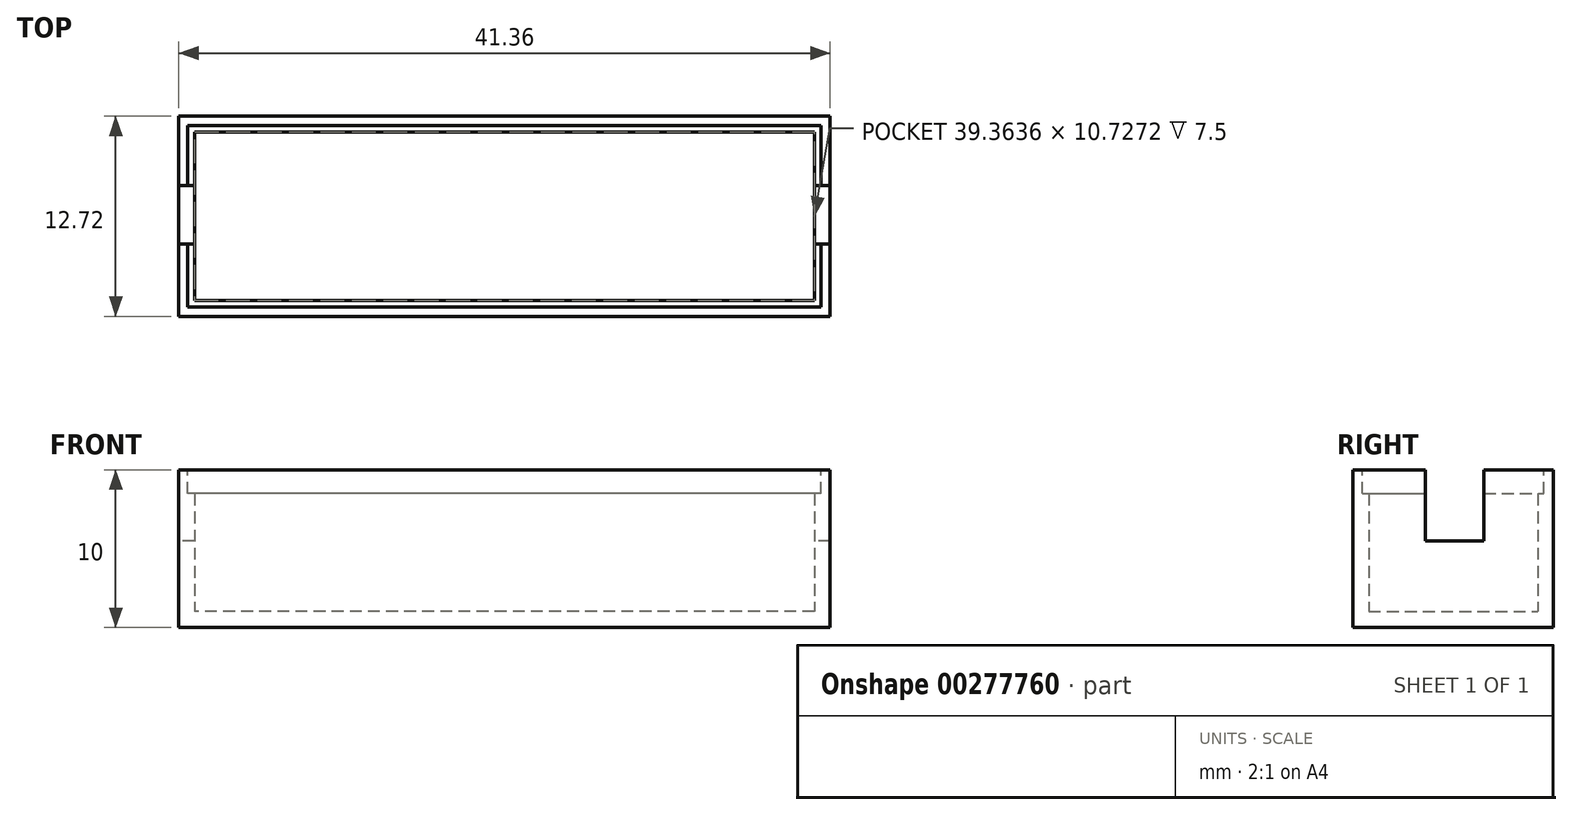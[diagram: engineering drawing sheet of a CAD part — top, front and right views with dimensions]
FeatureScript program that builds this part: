
annotation { "Feature Type Name" : "Feature", "Feature Type Description" : "" }
export const myFeature = defineFeature(function(context is Context, id is Id, definition is map)
    precondition{}
    {
        {
            var Q0;
            Q0=qCreatedBy(makeId("Top.planeOp"),FACE);
            var sketch = newSketch(context, id + "F0", { "sketchPlane" : qUnion([Q0])});
            skLineSegment(sketch, "E0.bottom", {"start": v(20.68, -6.36) * mm, "end": v(-20.68, -6.36) * mm});
            skLineSegment(sketch, "E0.top", {"start": v(20.68, 6.36) * mm, "end": v(-20.68, 6.36) * mm});
            skLineSegment(sketch, "E0.left", {"start": v(20.68, -6.36) * mm, "end": v(20.68, 6.36) * mm});
            skLineSegment(sketch, "E0.right", {"start": v(-20.68, -6.36) * mm, "end": v(-20.68, 6.36) * mm});
            skPoint(sketch, "E0.middle", {"position": v(0, 0) * mm});
            skSolve(sketch);
        }
        {
            var Q0;
            Q0 = qSketchRegion(id + "F0", true);
            extrude(context, id + "F1", {"entities" : qUnion([Q0]), "depth" : 10 * mm});
        }
        {
            var Q0;
            Q0=makeQuery(id+"F1.opExtrude","CAP_FACE",FACE,{"disambiguationData":[OSD([sQuery(id+"F0.wireOp",EDGE,"E0.bottom"),sQuery(id+"F0.wireOp",EDGE,"E0.top"),sQuery(id+"F0.wireOp",EDGE,"E0.left"),sQuery(id+"F0.wireOp",EDGE,"E0.right")])],"isStart":false});
            shell(context, id + "F2", {"entities" : qUnion([Q0]), "thickness" : 1 * mm});
        }
        {
            var Q0;
            Q0=makeQuery(id+"F1.opExtrude","CAP_FACE",FACE,{"disambiguationData":[OSD([sQuery(id+"F0.wireOp",EDGE,"E0.bottom"),sQuery(id+"F0.wireOp",EDGE,"E0.top"),sQuery(id+"F0.wireOp",EDGE,"E0.left"),sQuery(id+"F0.wireOp",EDGE,"E0.right")])],"isStart":false});
            var sketch = newSketch(context, id + "F3", { "sketchPlane" : qUnion([Q0])});
            skLineSegment(sketch, "E1.bottom", {"start": v(20.11, -5.77) * mm, "end": v(-20.11, -5.77) * mm});
            skLineSegment(sketch, "E1.top", {"start": v(20.11, 5.77) * mm, "end": v(-20.11, 5.77) * mm});
            skLineSegment(sketch, "E1.left", {"start": v(20.11, -5.77) * mm, "end": v(20.11, 5.77) * mm});
            skLineSegment(sketch, "E1.right", {"start": v(-20.11, -5.77) * mm, "end": v(-20.11, 5.77) * mm});
            skPoint(sketch, "E1.middle", {"position": v(0, 0) * mm});
            skSolve(sketch);
        }
        {
            var Q0;
            Q0 = qSketchRegion(id + "F3", true);
            extrude(context, id + "F4", {"entities" : qUnion([Q0]), "operationType" : NewBodyOperationType.REMOVE, "oppositeDirection" : true, "depth" : 1.5 * mm});
        }
        {
            var Q0;
            Q0=makeQuery(id+"F1.opExtrude","SWEPT_FACE",FACE,{"disambiguationData":[OSD([sQuery(id+"F0.wireOp",EDGE,"E0.right")])]});
            var sketch = newSketch(context, id + "F5", { "sketchPlane" : qUnion([Q0])});
            skLineSegment(sketch, "E2.bottom", {"start": v(-1.94, 10) * mm, "end": v(1.77, 10) * mm});
            skLineSegment(sketch, "E2.top", {"start": v(-1.94, 5.5) * mm, "end": v(1.77, 5.5) * mm});
            skLineSegment(sketch, "E2.left", {"start": v(-1.94, 10) * mm, "end": v(-1.94, 5.5) * mm});
            skLineSegment(sketch, "E2.right", {"start": v(1.77, 10) * mm, "end": v(1.77, 5.5) * mm});
            skSolve(sketch);
        }
        {
            var Q0;
            Q0 = qSketchRegion(id + "F5", true);
            extrude(context, id + "F6", {"entities" : qUnion([Q0]), "operationType" : NewBodyOperationType.REMOVE, "oppositeDirection" : true, "depth" : 60 * mm});
        }
    });
